# Revit family: Roof_Drain-Josam-21500-AE
name_source: partatom
category: Plumbing Fixtures
revit_build: Autodesk Revit MEP 2012 (Build: 20110309_2315(x64)
units: mm (PartAtom-declared; Revit-internal decimal feet)

## types (6) — shared parameters
04 CSI = 22 40 00
Color Availability = Green
Default Elevation = 48"
Description = Roof drain - cast iron
Extension Height = 1 1/2"
Inner Cleanout body = Metal - Josam - Brass - Satin
Manufacturer = Josam Company
Manufacturer Fax = 800-627-0008
Material = Cast Iron
Model = 21500-AE
Outer Cleanout Body = Metal - Josam - Anodized- Dark Bronze Satin
Product Line = Josam
Product Page URL = http://www.josam.com
Product Type = Large Sump
Subcategory = Roof Drain
Surface Finish = Painted
URL = http://www.josam.com
Weight = 59.00 lb

## per-type parameters (varying)
| type | Pipe Size Diameter | Pipe Size Radius |
| 2In Diameter | 2" | 1" |
| 3In Diameter | 3" | 1 1/2" |
| 4In Diameter | 4" | 2" |
| 5In Diameter | 5" | 2 1/2" |
| 6In Diameter | 6" | 3" |
| 8In Diameter | 8" | 4" |

## geometry (parser evidence)
native form markers: Blend x2, Sweep x8
no freeform markers — native parametric forms only
